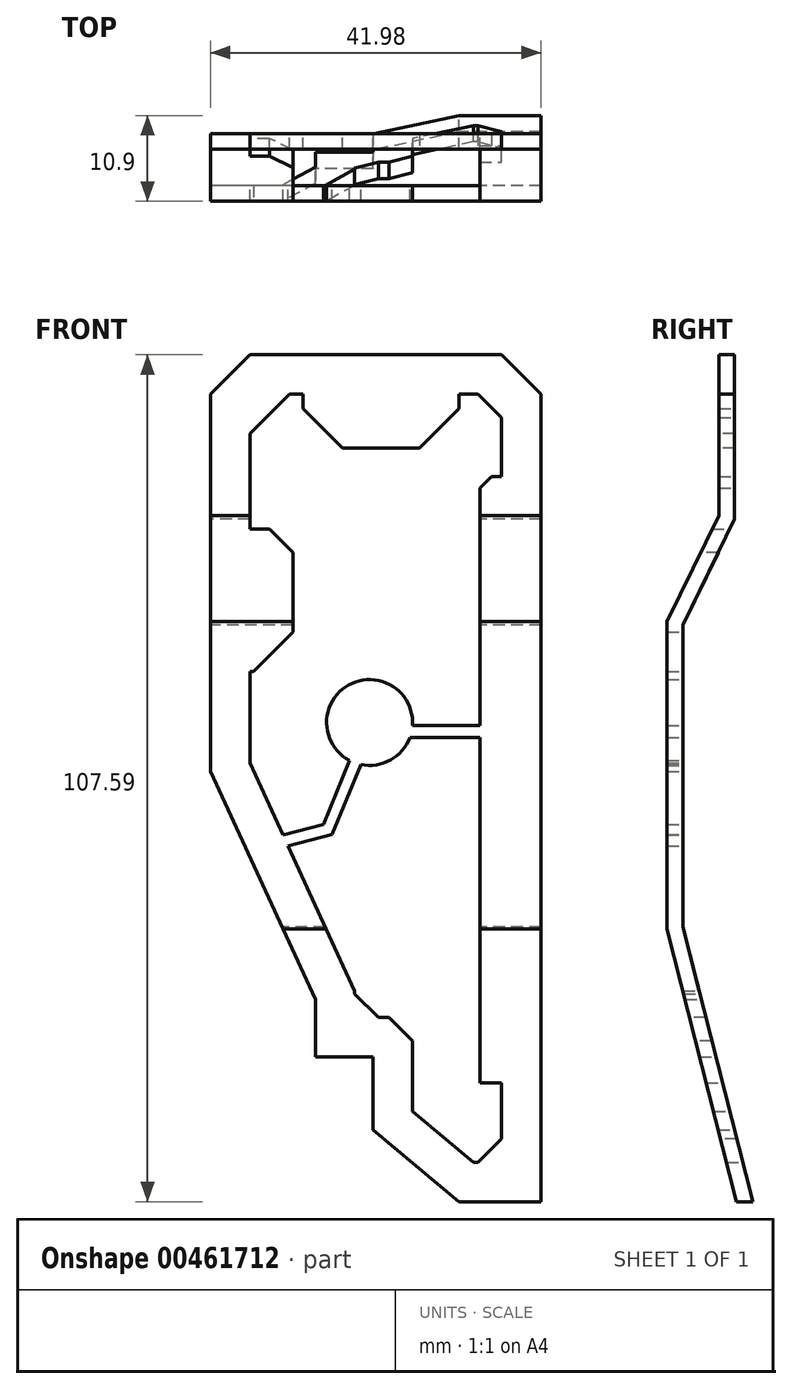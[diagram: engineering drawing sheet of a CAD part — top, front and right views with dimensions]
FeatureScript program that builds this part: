
annotation { "Feature Type Name" : "Feature", "Feature Type Description" : "" }
export const myFeature = defineFeature(function(context is Context, id is Id, definition is map)
    precondition{}
    {
        {
            var Q0;
            Q0=qCreatedBy(makeId("Front.planeOp"),FACE);
            var sketch = newSketch(context, id + "F0", { "sketchPlane" : qUnion([Q0])});
            skLineSegment(sketch, "E0", {"start": v(-31.56, 59.34) * mm, "end": v(-31.56, 0) * mm});
            skLineSegment(sketch, "E1", {"start": v(-31.56, 0) * mm, "end": v(-18.26, -28.95) * mm});
            skLineSegment(sketch, "E2", {"start": v(-18.26, -28.95) * mm, "end": v(-18.26, -36.23) * mm});
            skLineSegment(sketch, "E3", {"start": v(-18.26, -36.23) * mm, "end": v(-10.9, -36.23) * mm});
            skLineSegment(sketch, "E4", {"start": v(-10.9, -36.23) * mm, "end": v(-10.9, -45.5) * mm});
            skLineSegment(sketch, "E5", {"start": v(-10.9, -45.5) * mm, "end": v(0, -54.63) * mm});
            skLineSegment(sketch, "E6", {"start": v(0, -54.63) * mm, "end": v(10.42, -54.63) * mm});
            skLineSegment(sketch, "E7", {"start": v(10.42, -54.63) * mm, "end": v(10.42, 59.87) * mm});
            skLineSegment(sketch, "E8", {"start": v(-37.67, 52.96) * mm, "end": v(18.58, 52.96) * mm});
            skSolve(sketch);
        }
        {
            var Q0;
            Q0=qSketchRegion(id+"F0",true);
            extrude(context, id + "F1", {"entities" : qUnion([Q0]), "depth" : 25.4 * mm});
        }
        {
            var Q0;
            Q0=qCreatedBy(makeId("Front.planeOp"),FACE);
            var sketch = newSketch(context, id + "F2", { "sketchPlane" : qUnion([Q0])});
            skLineSegment(sketch, "E9.0", {"start": v(-26.56, 47.96) * mm, "end": v(-26.56, 1.1) * mm});
            skLineSegment(sketch, "E9.1", {"start": v(-26.56, 1.1) * mm, "end": v(-13.26, -27.86) * mm});
            skLineSegment(sketch, "E9.2", {"start": v(-26.56, 47.96) * mm, "end": v(5.42, 47.96) * mm});
            skLineSegment(sketch, "E9.3", {"start": v(-13.26, -27.86) * mm, "end": v(-13.26, -31.23) * mm});
            skLineSegment(sketch, "E9.4", {"start": v(-13.26, -31.23) * mm, "end": v(-5.9, -31.23) * mm});
            skLineSegment(sketch, "E9.5", {"start": v(5.42, -49.63) * mm, "end": v(5.42, 47.96) * mm});
            skLineSegment(sketch, "E9.6", {"start": v(1.82, -49.63) * mm, "end": v(5.42, -49.63) * mm});
            skLineSegment(sketch, "E9.7", {"start": v(-5.9, -43.16) * mm, "end": v(1.82, -49.63) * mm});
            skLineSegment(sketch, "E9.8", {"start": v(-5.9, -31.23) * mm, "end": v(-5.9, -43.16) * mm});
            skLineSegment(sketch, "E10.bottom", {"start": v(-19.8, 63.96) * mm, "end": v(0, 63.96) * mm});
            skLineSegment(sketch, "E10.top", {"start": v(-19.8, 41.13) * mm, "end": v(0, 41.13) * mm});
            skLineSegment(sketch, "E10.left", {"start": v(-19.8, 63.96) * mm, "end": v(-19.8, 41.13) * mm});
            skLineSegment(sketch, "E10.right", {"start": v(0, 63.96) * mm, "end": v(0, 41.13) * mm});
            skLineSegment(sketch, "E11.bottom", {"start": v(-36.17, 30.84) * mm, "end": v(-21.1, 30.84) * mm});
            skLineSegment(sketch, "E11.top", {"start": v(-36.17, 12.73) * mm, "end": v(-21.1, 12.73) * mm});
            skLineSegment(sketch, "E11.left", {"start": v(-36.17, 30.84) * mm, "end": v(-36.17, 12.73) * mm});
            skLineSegment(sketch, "E11.right", {"start": v(-21.1, 30.84) * mm, "end": v(-21.1, 12.73) * mm});
            skLineSegment(sketch, "E12.bottom", {"start": v(15.3, -39.52) * mm, "end": v(2.65, -39.52) * mm});
            skLineSegment(sketch, "E12.top", {"start": v(15.3, 37.5) * mm, "end": v(2.65, 37.5) * mm});
            skLineSegment(sketch, "E12.left", {"start": v(15.3, -39.52) * mm, "end": v(15.3, 37.5) * mm});
            skLineSegment(sketch, "E12.right", {"start": v(2.65, -39.52) * mm, "end": v(2.65, 37.5) * mm});
            skCircle(sketch, "E13", {"center": v(-11.36, 6.24) * mm, "radius": 5.46 * mm});
            skLineSegment(sketch, "E14", {"start": v(-29.17, -9.83) * mm, "end": v(-17.21, -6.7) * mm});
            skLineSegment(sketch, "E15", {"start": v(-17.21, -6.7) * mm, "end": v(-12.54, 4.7) * mm});
            skLineSegment(sketch, "E16", {"start": v(-9.3, 5.86) * mm, "end": v(5.42, 5.86) * mm});
            skLineSegment(sketch, "E17.0", {"start": v(-16.11, -7.97) * mm, "end": v(-11.15, 4.13) * mm});
            skLineSegment(sketch, "E17.1", {"start": v(-28.8, -11.29) * mm, "end": v(-16.11, -7.97) * mm});
            skLineSegment(sketch, "E18.0", {"start": v(-9.3, 4.36) * mm, "end": v(5.42, 4.36) * mm});
            skLineSegment(sketch, "E19", {"start": v(-12.54, 4.7) * mm, "end": v(-11.15, 4.13) * mm});
            skLineSegment(sketch, "E20", {"start": v(-9.3, 5.86) * mm, "end": v(-9.3, 4.36) * mm});
            skLineSegment(sketch, "E21", {"start": v(-29.17, -9.83) * mm, "end": v(-29.17, -9.83) * mm});
            skLineSegment(sketch, "E22", {"start": v(-29.17, -9.83) * mm, "end": v(-28.8, -11.29) * mm});
            skLineSegment(sketch, "E23", {"start": v(5.42, 5.86) * mm, "end": v(5.42, 4.36) * mm});
            skSolve(sketch);
        }
        {
            var Q0;
            {var subQ1=sQuery(id+"F2.wireOp",EDGE,"E10.top");Q0=makeQuery(id+"F2.imprint","IMPRINT",FACE,{"disambiguationData":[TD([[makeQuery(id+"F2.imprint","IMPRINT",EDGE,{"derivedFrom":subQ1}),-1.0]])]});}
            extrude(context, id + "F3", {"entities" : qUnion([Q0]), "endBound" : BoundingType.SYMMETRIC, "depth" : 60 * mm});
        }
        {
            var Q0;
            {var subQ10=sQuery(id+"F2.wireOp",EDGE,"E9.3");Q0=makeQuery(id+"F2.imprint","IMPRINT",FACE,{"disambiguationData":[TD([[makeQuery(id+"F2.imprint","IMPRINT",EDGE,{"derivedFrom":subQ10}),1.0]])]});}
            extrude(context, id + "F4", {"entities" : qUnion([Q0]), "endBound" : BoundingType.SYMMETRIC, "depth" : 60 * mm});
        }
        {
            var Q0;
            Q0=makeQuery(id+"F3.opExtrude","SWEPT_BODY",BODY,{"disambiguationData":[OSD([sQuery(id+"F2.wireOp",EDGE,"E9.0"),sQuery(id+"F2.wireOp",EDGE,"E9.1"),sQuery(id+"F2.wireOp",EDGE,"E9.2"),sQuery(id+"F2.wireOp",EDGE,"E9.5"),sQuery(id+"F2.wireOp",EDGE,"E10.top"),sQuery(id+"F2.wireOp",EDGE,"E10.left"),sQuery(id+"F2.wireOp",EDGE,"E10.right"),sQuery(id+"F2.wireOp",EDGE,"E11.bottom"),sQuery(id+"F2.wireOp",EDGE,"E11.top"),sQuery(id+"F2.wireOp",EDGE,"E11.right"),sQuery(id+"F2.wireOp",EDGE,"E12.top"),sQuery(id+"F2.wireOp",EDGE,"E12.right"),sQuery(id+"F2.wireOp",EDGE,"E13"),sQuery(id+"F2.wireOp",EDGE,"E14"),sQuery(id+"F2.wireOp",EDGE,"E15"),sQuery(id+"F2.wireOp",EDGE,"E16")])]});
            var Q1;
            Q1=makeQuery(id+"F1.opExtrude","SWEPT_BODY",BODY,{"disambiguationData":[OSD([sQuery(id+"F0.wireOp",EDGE,"E0"),sQuery(id+"F0.wireOp",EDGE,"E1"),sQuery(id+"F0.wireOp",EDGE,"E2"),sQuery(id+"F0.wireOp",EDGE,"E3"),sQuery(id+"F0.wireOp",EDGE,"E4"),sQuery(id+"F0.wireOp",EDGE,"E5"),sQuery(id+"F0.wireOp",EDGE,"E6"),sQuery(id+"F0.wireOp",EDGE,"E7"),sQuery(id+"F0.wireOp",EDGE,"E8")])]});
            booleanBodies(context, id + "F5", {"operationType" : BooleanOperationType.SUBTRACTION, "tools" : qUnion([Q0]), "targets" : qUnion([Q1])});
        }
        {
            var Q0;
            Q0=makeQuery(id+"F4.opExtrude","SWEPT_BODY",BODY,{"disambiguationData":[OSD([sQuery(id+"F2.wireOp",EDGE,"E9.1"),sQuery(id+"F2.wireOp",EDGE,"E9.3"),sQuery(id+"F2.wireOp",EDGE,"E9.4"),sQuery(id+"F2.wireOp",EDGE,"E9.5"),sQuery(id+"F2.wireOp",EDGE,"E9.6"),sQuery(id+"F2.wireOp",EDGE,"E9.7"),sQuery(id+"F2.wireOp",EDGE,"E9.8"),sQuery(id+"F2.wireOp",EDGE,"E12.bottom"),sQuery(id+"F2.wireOp",EDGE,"E12.right"),sQuery(id+"F2.wireOp",EDGE,"E13"),sQuery(id+"F2.wireOp",EDGE,"E17.0"),sQuery(id+"F2.wireOp",EDGE,"E17.1"),sQuery(id+"F2.wireOp",EDGE,"E18.0")])]});
            var Q1;
            Q1=makeQuery(id+"F1.opExtrude","SWEPT_BODY",BODY,{"disambiguationData":[OSD([sQuery(id+"F0.wireOp",EDGE,"E0"),sQuery(id+"F0.wireOp",EDGE,"E1"),sQuery(id+"F0.wireOp",EDGE,"E2"),sQuery(id+"F0.wireOp",EDGE,"E3"),sQuery(id+"F0.wireOp",EDGE,"E4"),sQuery(id+"F0.wireOp",EDGE,"E5"),sQuery(id+"F0.wireOp",EDGE,"E6"),sQuery(id+"F0.wireOp",EDGE,"E7"),sQuery(id+"F0.wireOp",EDGE,"E8")])]});
            booleanBodies(context, id + "F6", {"operationType" : BooleanOperationType.SUBTRACTION, "tools" : qUnion([Q0]), "targets" : qUnion([Q1])});
        }
        {
            var Q0;
            Q0=makeQuery(id+"F1.opExtrude","CAP_FACE",FACE,{"disambiguationData":[OSD([sQuery(id+"F0.wireOp",EDGE,"E0"),sQuery(id+"F0.wireOp",EDGE,"E1"),sQuery(id+"F0.wireOp",EDGE,"E2"),sQuery(id+"F0.wireOp",EDGE,"E3"),sQuery(id+"F0.wireOp",EDGE,"E4"),sQuery(id+"F0.wireOp",EDGE,"E5"),sQuery(id+"F0.wireOp",EDGE,"E6"),sQuery(id+"F0.wireOp",EDGE,"E7"),sQuery(id+"F0.wireOp",EDGE,"E8")])],"isStart":true});
            extrude(context, id + "F7", {"entities" : qUnion([Q0]), "operationType" : NewBodyOperationType.ADD, "depth" : 25 * mm});
        }
        {
            var Q0;
            Q0=qCreatedBy(makeId("Right.planeOp"),FACE);
            var sketch = newSketch(context, id + "F8", { "sketchPlane" : qUnion([Q0])});
            skLineSegment(sketch, "E24", {"start": v(-5.44, 63.21) * mm, "end": v(-5.44, 32.1) * mm});
            skLineSegment(sketch, "E25", {"start": v(-5.44, 32.1) * mm, "end": v(-12.03, 18.6) * mm});
            skLineSegment(sketch, "E26", {"start": v(-12.03, 18.6) * mm, "end": v(-12.03, -19.71) * mm});
            skLineSegment(sketch, "E27", {"start": v(-12.03, -19.71) * mm, "end": v(-1.98, -59.15) * mm});
            skLineSegment(sketch, "E28.0", {"start": v(-14.03, -19.96) * mm, "end": v(-3.92, -59.64) * mm});
            skLineSegment(sketch, "E28.1", {"start": v(-14.03, 19.06) * mm, "end": v(-14.03, -19.96) * mm});
            skLineSegment(sketch, "E28.2", {"start": v(-7.44, 32.55) * mm, "end": v(-14.03, 19.06) * mm});
            skLineSegment(sketch, "E28.3", {"start": v(-7.44, 63.21) * mm, "end": v(-7.44, 32.55) * mm});
            skLineSegment(sketch, "E29", {"start": v(-5.44, 63.21) * mm, "end": v(-7.44, 63.21) * mm});
            skLineSegment(sketch, "E30", {"start": v(-1.98, -59.15) * mm, "end": v(-3.92, -59.64) * mm});
            skSolve(sketch);
        }
        {
            var Q0;
            Q0=makeQuery(id+"F8.imprint","IMPRINT",FACE,{"disambiguationData":[TD([[makeQuery(id+"F8.imprint","IMPRINT",EDGE,{"derivedFrom":sQuery(id+"F8.wireOp",EDGE,"E24")}),-1.0]])]});
            extrude(context, id + "F9", {"entities" : qUnion([Q0]), "endBound" : BoundingType.SYMMETRIC, "depth" : 80 * mm});
        }
        {
            var Q0;
            Q0=makeQuery(id+"F1.opExtrude","SWEPT_BODY",BODY,{"disambiguationData":[OSD([sQuery(id+"F0.wireOp",EDGE,"E0"),sQuery(id+"F0.wireOp",EDGE,"E1"),sQuery(id+"F0.wireOp",EDGE,"E2"),sQuery(id+"F0.wireOp",EDGE,"E3"),sQuery(id+"F0.wireOp",EDGE,"E4"),sQuery(id+"F0.wireOp",EDGE,"E5"),sQuery(id+"F0.wireOp",EDGE,"E6"),sQuery(id+"F0.wireOp",EDGE,"E7"),sQuery(id+"F0.wireOp",EDGE,"E8")])]});
            var Q1;
            Q1=makeQuery(id+"F9.opExtrude","SWEPT_BODY",BODY,{"disambiguationData":[OSD([sQuery(id+"F8.wireOp",EDGE,"E24"),sQuery(id+"F8.wireOp",EDGE,"E25"),sQuery(id+"F8.wireOp",EDGE,"E26"),sQuery(id+"F8.wireOp",EDGE,"E27"),sQuery(id+"F8.wireOp",EDGE,"E28.0"),sQuery(id+"F8.wireOp",EDGE,"E28.1"),sQuery(id+"F8.wireOp",EDGE,"E28.2"),sQuery(id+"F8.wireOp",EDGE,"E28.3"),sQuery(id+"F8.wireOp",EDGE,"E29"),sQuery(id+"F8.wireOp",EDGE,"E30")])]});
            booleanBodies(context, id + "F10", {"operationType" : BooleanOperationType.INTERSECTION, "tools" : qUnion([Q0, Q1])});
        }
        {
            var Q0;
            {var subQ0=sQuery(id+"F2.wireOp",EDGE,"E9.2");var subQ1=sQuery(id+"F2.wireOp",EDGE,"E9.0");Q0=makeQuery(id+"F7.boolean.opBoolean","MERGE",EDGE,{"derivedFrom":[makeQuery(id+"F5.opBoolean","COPY",EDGE,{"derivedFrom":makeQuery(id+"F3.opExtrude","SWEPT_EDGE",EDGE,{"disambiguationData":[OSD([subQ1,subQ0])]})}),makeQuery(id+"F7.opExtrude","SWEPT_EDGE",EDGE,{"disambiguationData":[OSD([sQuery(id+"F0.wireOp",EDGE,"E0"),sQuery(id+"F0.wireOp",EDGE,"E1"),sQuery(id+"F0.wireOp",EDGE,"E2"),sQuery(id+"F0.wireOp",EDGE,"E3"),sQuery(id+"F0.wireOp",EDGE,"E4"),sQuery(id+"F0.wireOp",EDGE,"E5"),sQuery(id+"F0.wireOp",EDGE,"E6"),sQuery(id+"F0.wireOp",EDGE,"E7"),sQuery(id+"F0.wireOp",EDGE,"E8"),subQ1,subQ0])]})]});}
            var Q1;
            {var subQ0=sQuery(id+"F2.wireOp",EDGE,"E10.right");var subQ1=sQuery(id+"F2.wireOp",EDGE,"E10.top");Q1=makeQuery(id+"F7.boolean.opBoolean","MERGE",EDGE,{"derivedFrom":[makeQuery(id+"F5.opBoolean","COPY",EDGE,{"derivedFrom":makeQuery(id+"F3.opExtrude","SWEPT_EDGE",EDGE,{"disambiguationData":[OSD([subQ1,subQ0])]})}),makeQuery(id+"F7.opExtrude","SWEPT_EDGE",EDGE,{"disambiguationData":[OSD([sQuery(id+"F0.wireOp",EDGE,"E0"),sQuery(id+"F0.wireOp",EDGE,"E1"),sQuery(id+"F0.wireOp",EDGE,"E2"),sQuery(id+"F0.wireOp",EDGE,"E3"),sQuery(id+"F0.wireOp",EDGE,"E4"),sQuery(id+"F0.wireOp",EDGE,"E5"),sQuery(id+"F0.wireOp",EDGE,"E6"),sQuery(id+"F0.wireOp",EDGE,"E7"),sQuery(id+"F0.wireOp",EDGE,"E8"),subQ1,subQ0])]})]});}
            var Q2;
            {var subQ0=sQuery(id+"F2.wireOp",EDGE,"E10.left");var subQ1=sQuery(id+"F2.wireOp",EDGE,"E10.top");Q2=makeQuery(id+"F7.boolean.opBoolean","MERGE",EDGE,{"derivedFrom":[makeQuery(id+"F5.opBoolean","COPY",EDGE,{"derivedFrom":makeQuery(id+"F3.opExtrude","SWEPT_EDGE",EDGE,{"disambiguationData":[OSD([subQ1,subQ0])]})}),makeQuery(id+"F7.opExtrude","SWEPT_EDGE",EDGE,{"disambiguationData":[OSD([sQuery(id+"F0.wireOp",EDGE,"E0"),sQuery(id+"F0.wireOp",EDGE,"E1"),sQuery(id+"F0.wireOp",EDGE,"E2"),sQuery(id+"F0.wireOp",EDGE,"E3"),sQuery(id+"F0.wireOp",EDGE,"E4"),sQuery(id+"F0.wireOp",EDGE,"E5"),sQuery(id+"F0.wireOp",EDGE,"E6"),sQuery(id+"F0.wireOp",EDGE,"E7"),sQuery(id+"F0.wireOp",EDGE,"E8"),subQ1,subQ0])]})]});}
            var Q3;
            {var subQ0=sQuery(id+"F2.wireOp",EDGE,"E11.right");var subQ1=sQuery(id+"F2.wireOp",EDGE,"E11.top");Q3=makeQuery(id+"F7.boolean.opBoolean","MERGE",EDGE,{"derivedFrom":[makeQuery(id+"F5.opBoolean","COPY",EDGE,{"derivedFrom":makeQuery(id+"F3.opExtrude","SWEPT_EDGE",EDGE,{"disambiguationData":[OSD([subQ1,subQ0])]})}),makeQuery(id+"F7.opExtrude","SWEPT_EDGE",EDGE,{"disambiguationData":[OSD([sQuery(id+"F0.wireOp",EDGE,"E0"),sQuery(id+"F0.wireOp",EDGE,"E1"),sQuery(id+"F0.wireOp",EDGE,"E2"),sQuery(id+"F0.wireOp",EDGE,"E3"),sQuery(id+"F0.wireOp",EDGE,"E4"),sQuery(id+"F0.wireOp",EDGE,"E5"),sQuery(id+"F0.wireOp",EDGE,"E6"),sQuery(id+"F0.wireOp",EDGE,"E7"),sQuery(id+"F0.wireOp",EDGE,"E8"),subQ1,subQ0])]})]});}
            chamfer(context, id + "F11", {"entities" : qUnion([Q0, Q1, Q2, Q3]), "width" : 5 * mm, "tangentPropagation" : true});
        }
        {
            var Q0;
            {var subQ0=sQuery(id+"F2.wireOp",EDGE,"E9.5");var subQ1=sQuery(id+"F2.wireOp",EDGE,"E9.2");Q0=makeQuery(id+"F7.boolean.opBoolean","MERGE",EDGE,{"derivedFrom":[makeQuery(id+"F5.opBoolean","COPY",EDGE,{"derivedFrom":makeQuery(id+"F3.opExtrude","SWEPT_EDGE",EDGE,{"disambiguationData":[OSD([subQ1,subQ0])]})}),makeQuery(id+"F7.opExtrude","SWEPT_EDGE",EDGE,{"disambiguationData":[OSD([sQuery(id+"F0.wireOp",EDGE,"E0"),sQuery(id+"F0.wireOp",EDGE,"E1"),sQuery(id+"F0.wireOp",EDGE,"E2"),sQuery(id+"F0.wireOp",EDGE,"E3"),sQuery(id+"F0.wireOp",EDGE,"E4"),sQuery(id+"F0.wireOp",EDGE,"E5"),sQuery(id+"F0.wireOp",EDGE,"E6"),sQuery(id+"F0.wireOp",EDGE,"E7"),sQuery(id+"F0.wireOp",EDGE,"E8"),subQ1,subQ0])]})]});}
            var Q1;
            {var subQ0=sQuery(id+"F2.wireOp",EDGE,"E11.right");var subQ1=sQuery(id+"F2.wireOp",EDGE,"E11.bottom");Q1=makeQuery(id+"F7.boolean.opBoolean","MERGE",EDGE,{"derivedFrom":[makeQuery(id+"F5.opBoolean","COPY",EDGE,{"derivedFrom":makeQuery(id+"F3.opExtrude","SWEPT_EDGE",EDGE,{"disambiguationData":[OSD([subQ1,subQ0])]})}),makeQuery(id+"F7.opExtrude","SWEPT_EDGE",EDGE,{"disambiguationData":[OSD([sQuery(id+"F0.wireOp",EDGE,"E0"),sQuery(id+"F0.wireOp",EDGE,"E1"),sQuery(id+"F0.wireOp",EDGE,"E2"),sQuery(id+"F0.wireOp",EDGE,"E3"),sQuery(id+"F0.wireOp",EDGE,"E4"),sQuery(id+"F0.wireOp",EDGE,"E5"),sQuery(id+"F0.wireOp",EDGE,"E6"),sQuery(id+"F0.wireOp",EDGE,"E7"),sQuery(id+"F0.wireOp",EDGE,"E8"),subQ1,subQ0])]})]});}
            var Q2;
            {var subQ0=sQuery(id+"F2.wireOp",EDGE,"E9.6");var subQ1=sQuery(id+"F2.wireOp",EDGE,"E9.5");Q2=makeQuery(id+"F7.boolean.opBoolean","MERGE",EDGE,{"derivedFrom":[makeQuery(id+"F6.opBoolean","COPY",EDGE,{"derivedFrom":makeQuery(id+"F4.opExtrude","SWEPT_EDGE",EDGE,{"disambiguationData":[OSD([subQ1,subQ0])]})}),makeQuery(id+"F7.opExtrude","SWEPT_EDGE",EDGE,{"disambiguationData":[OSD([sQuery(id+"F0.wireOp",EDGE,"E0"),sQuery(id+"F0.wireOp",EDGE,"E1"),sQuery(id+"F0.wireOp",EDGE,"E2"),sQuery(id+"F0.wireOp",EDGE,"E3"),sQuery(id+"F0.wireOp",EDGE,"E4"),sQuery(id+"F0.wireOp",EDGE,"E5"),sQuery(id+"F0.wireOp",EDGE,"E6"),sQuery(id+"F0.wireOp",EDGE,"E7"),sQuery(id+"F0.wireOp",EDGE,"E8"),subQ1,subQ0])]})]});}
            var Q3;
            {var subQ0=sQuery(id+"F2.wireOp",EDGE,"E9.8");var subQ1=sQuery(id+"F2.wireOp",EDGE,"E9.4");Q3=makeQuery(id+"F7.boolean.opBoolean","MERGE",EDGE,{"derivedFrom":[makeQuery(id+"F6.opBoolean","COPY",EDGE,{"derivedFrom":makeQuery(id+"F4.opExtrude","SWEPT_EDGE",EDGE,{"disambiguationData":[OSD([subQ1,subQ0])]})}),makeQuery(id+"F7.opExtrude","SWEPT_EDGE",EDGE,{"disambiguationData":[OSD([sQuery(id+"F0.wireOp",EDGE,"E0"),sQuery(id+"F0.wireOp",EDGE,"E1"),sQuery(id+"F0.wireOp",EDGE,"E2"),sQuery(id+"F0.wireOp",EDGE,"E3"),sQuery(id+"F0.wireOp",EDGE,"E4"),sQuery(id+"F0.wireOp",EDGE,"E5"),sQuery(id+"F0.wireOp",EDGE,"E6"),sQuery(id+"F0.wireOp",EDGE,"E7"),sQuery(id+"F0.wireOp",EDGE,"E8"),subQ1,subQ0])]})]});}
            var Q4;
            {var subQ0=sQuery(id+"F2.wireOp",EDGE,"E9.4");var subQ1=sQuery(id+"F2.wireOp",EDGE,"E9.3");Q4=makeQuery(id+"F7.boolean.opBoolean","MERGE",EDGE,{"derivedFrom":[makeQuery(id+"F6.opBoolean","COPY",EDGE,{"derivedFrom":makeQuery(id+"F4.opExtrude","SWEPT_EDGE",EDGE,{"disambiguationData":[OSD([subQ1,subQ0])]})}),makeQuery(id+"F7.opExtrude","SWEPT_EDGE",EDGE,{"disambiguationData":[OSD([sQuery(id+"F0.wireOp",EDGE,"E0"),sQuery(id+"F0.wireOp",EDGE,"E1"),sQuery(id+"F0.wireOp",EDGE,"E2"),sQuery(id+"F0.wireOp",EDGE,"E3"),sQuery(id+"F0.wireOp",EDGE,"E4"),sQuery(id+"F0.wireOp",EDGE,"E5"),sQuery(id+"F0.wireOp",EDGE,"E6"),sQuery(id+"F0.wireOp",EDGE,"E7"),sQuery(id+"F0.wireOp",EDGE,"E8"),subQ1,subQ0])]})]});}
            chamfer(context, id + "F12", {"entities" : qUnion([Q0, Q1, Q2, Q3, Q4]), "width" : 3 * mm, "tangentPropagation" : true});
        }
        {
            var Q0;
            {var subQ0=sQuery(id+"F2.wireOp",EDGE,"E12.right");var subQ1=sQuery(id+"F2.wireOp",EDGE,"E12.top");Q0=makeQuery(id+"F7.boolean.opBoolean","MERGE",EDGE,{"derivedFrom":[makeQuery(id+"F5.opBoolean","COPY",EDGE,{"derivedFrom":makeQuery(id+"F3.opExtrude","SWEPT_EDGE",EDGE,{"disambiguationData":[OSD([subQ1,subQ0])]})}),makeQuery(id+"F7.opExtrude","SWEPT_EDGE",EDGE,{"disambiguationData":[OSD([sQuery(id+"F0.wireOp",EDGE,"E0"),sQuery(id+"F0.wireOp",EDGE,"E1"),sQuery(id+"F0.wireOp",EDGE,"E2"),sQuery(id+"F0.wireOp",EDGE,"E3"),sQuery(id+"F0.wireOp",EDGE,"E4"),sQuery(id+"F0.wireOp",EDGE,"E5"),sQuery(id+"F0.wireOp",EDGE,"E6"),sQuery(id+"F0.wireOp",EDGE,"E7"),sQuery(id+"F0.wireOp",EDGE,"E8"),subQ1,subQ0])]})]});}
            chamfer(context, id + "F13", {"entities" : qUnion([Q0]), "width" : 1.5 * mm, "tangentPropagation" : true});
        }
        {
            var Q0;
            {var subQ0=sQuery(id+"F0.wireOp",EDGE,"E8");var subQ1=sQuery(id+"F0.wireOp",EDGE,"E7");Q0=makeQuery(id+"F7.boolean.opBoolean","MERGE",EDGE,{"derivedFrom":[makeQuery(id+"F1.opExtrude","SWEPT_EDGE",EDGE,{"disambiguationData":[OSD([subQ1,subQ0])]}),makeQuery(id+"F7.opExtrude","SWEPT_EDGE",EDGE,{"disambiguationData":[OSD([subQ1,subQ0])]})]});}
            var Q1;
            {var subQ0=sQuery(id+"F0.wireOp",EDGE,"E8");var subQ1=sQuery(id+"F0.wireOp",EDGE,"E0");Q1=makeQuery(id+"F7.boolean.opBoolean","MERGE",EDGE,{"derivedFrom":[makeQuery(id+"F1.opExtrude","SWEPT_EDGE",EDGE,{"disambiguationData":[OSD([subQ1,subQ0])]}),makeQuery(id+"F7.opExtrude","SWEPT_EDGE",EDGE,{"disambiguationData":[OSD([subQ1,subQ0])]})]});}
            chamfer(context, id + "F14", {"entities" : qUnion([Q0, Q1]), "width" : 5 * mm, "tangentPropagation" : true});
        }
    });
